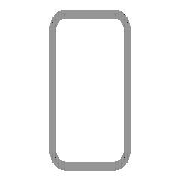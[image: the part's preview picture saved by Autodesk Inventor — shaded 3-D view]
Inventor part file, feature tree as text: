
AUTODESK INVENTOR PART (.ipt)
format: ipt  version: 2025 (Build 290162010, 162A)  size: 132,608 bytes
history: native  units: mm (DEFAULTED — no unit token found)
features: other x4, sketch x1, plane x1
ambient origin geometry x8: Origin, YZ Plane, XZ Plane, XY Plane, X Axis, Y Axis, Z Axis, Center Point
bodies: Solid1 (feature_tree), Body (feature_tree)
feature tree (6):
  parser-record x1  (decoder bookkeeping rows leaked as tree rows — omitted from the tree; the rows remain in map.json)
  other  "Driven Length"
  other  "Start Plane"
  other  "End Plane"
  sketch  "Sketch3"  dims[d3=814.0mm d4=0.0mm d7=6.0mm d9=40.0mm d11=60.0mm d12=3.0mm d13=-0.0mm d14=814.0mm d15=20.0mm d16=30.0mm d17=90.0deg d18=814.0mm]
  plane  "Work Plane3"
